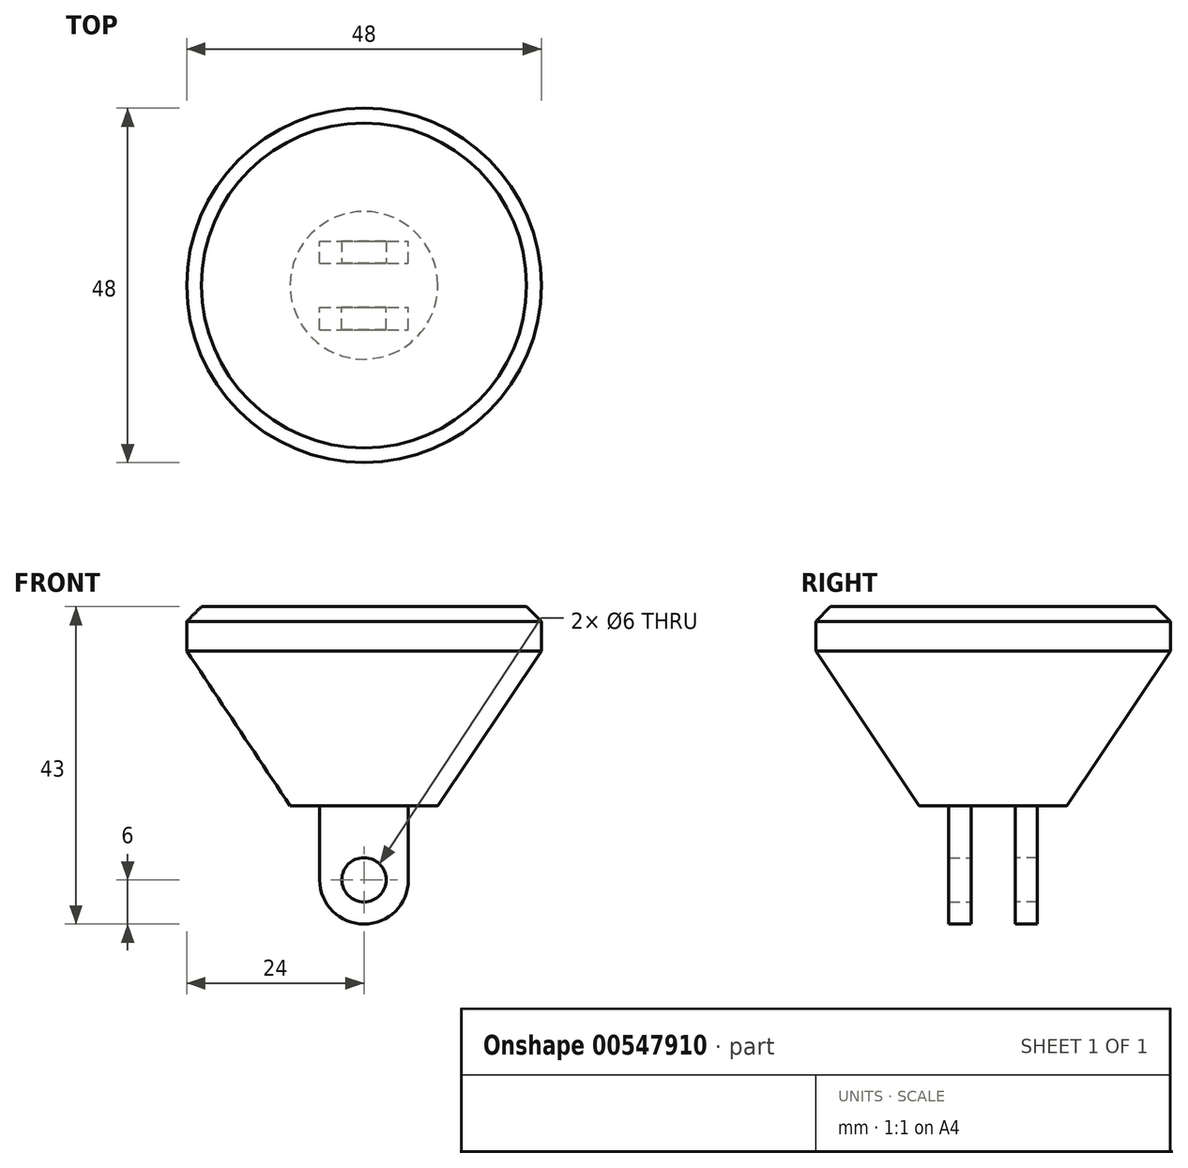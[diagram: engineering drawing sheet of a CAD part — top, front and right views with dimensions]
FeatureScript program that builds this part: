
annotation { "Feature Type Name" : "Feature", "Feature Type Description" : "" }
export const myFeature = defineFeature(function(context is Context, id is Id, definition is map)
    precondition{}
    {
        {
            var Q0;
            Q0=qCreatedBy(makeId("Front.planeOp"),FACE);
            var sketch = newSketch(context, id + "F0", { "sketchPlane" : qUnion([Q0])});
            skLineSegment(sketch, "E0", {"start": v(0, 0) * mm, "end": v(0, 27) * mm});
            skLineSegment(sketch, "E1", {"start": v(0, 27) * mm, "end": v(24, 27) * mm});
            skLineSegment(sketch, "E2", {"start": v(24, 27) * mm, "end": v(24, 21) * mm});
            skLineSegment(sketch, "E3", {"start": v(24, 21) * mm, "end": v(10, 0) * mm});
            skLineSegment(sketch, "E4", {"start": v(10, 0) * mm, "end": v(0, 0) * mm});
            skSolve(sketch);
        }
        {
            var Q0;
            Q0=makeQuery(id+"F0.imprint","IMPRINT",FACE,{"disambiguationData":[TD([[makeQuery(id+"F0.imprint","IMPRINT",EDGE,{"derivedFrom":sQuery(id+"F0.wireOp",EDGE,"E0")}),-1.0]])]});
            var Q1;
            Q1=sQuery(id+"F0.wireOp",EDGE,"E0");
            revolve(context, id + "F1", {"entities" : qUnion([Q0]), "axis" : qUnion([Q1]), "revolveType" : RevolveType.FULL});
        }
        {
            var Q0;
            Q0=qCreatedBy(makeId("Front.planeOp"),FACE);
            var sketch = newSketch(context, id + "F2", { "sketchPlane" : qUnion([Q0])});
            skLineSegment(sketch, "E5", {"start": v(6, 0) * mm, "end": v(6, -10) * mm});
            skArc(sketch, "E6", {"start": v(-6, -10) * mm, "mid": v(0, -16) * mm, "end": v(6, -10) * mm});
            skLineSegment(sketch, "E7", {"start": v(-6, -10) * mm, "end": v(-6, 0) * mm});
            skLineSegment(sketch, "E8", {"start": v(-6, 0) * mm, "end": v(6, 0) * mm});
            skSolve(sketch);
        }
        {
            var Q0;
            Q0=makeQuery(id+"F2.imprint","IMPRINT",FACE,{"disambiguationData":[TD([[makeQuery(id+"F2.imprint","IMPRINT",EDGE,{"derivedFrom":sQuery(id+"F2.wireOp",EDGE,"E5")}),-1.0]])]});
            extrude(context, id + "F3", {"entities" : qUnion([Q0]), "operationType" : NewBodyOperationType.ADD, "endBound" : BoundingType.SYMMETRIC, "depth" : 12 * mm, "offsetDistance" : 25 * mm});
        }
        {
            var Q0;
            Q0 = qSketchRegion(id + "F2", true);
            extrude(context, id + "F4", {"entities" : qUnion([Q0]), "operationType" : NewBodyOperationType.REMOVE, "endBound" : BoundingType.SYMMETRIC, "oppositeDirection" : true, "depth" : 6 * mm, "offsetDistance" : 25 * mm});
        }
        {
            var Q0;
            Q0=sQuery(id+"F2.wireOp",VERTEX,"E6.center");
            var Q1;
            Q1=makeQuery(id+"F1.opRevolve","SWEPT_BODY",BODY,{"disambiguationData":[OSD([sQuery(id+"F0.wireOp",EDGE,"E0"),sQuery(id+"F0.wireOp",EDGE,"E1"),sQuery(id+"F0.wireOp",EDGE,"E2"),sQuery(id+"F0.wireOp",EDGE,"E3"),sQuery(id+"F0.wireOp",EDGE,"E4")])]});
            hole(context, id + "F5", {"style" : HoleStyle.SIMPLE, "endStyle" : HoleEndStyle.THROUGH, "holeDiameter" : 6 * mm, "isTappedThrough" : true, "tappedDepth" : 12 * mm, "tapClearance" : 3, "locations" : qUnion([Q0]), "scope" : qUnion([Q1])});
        }
        {
            var Q0;
            Q0=sQuery(id+"F2.wireOp",VERTEX,"E6.center");
            var Q1;
            Q1=makeQuery(id+"F1.opRevolve","SWEPT_BODY",BODY,{"disambiguationData":[OSD([sQuery(id+"F0.wireOp",EDGE,"E0"),sQuery(id+"F0.wireOp",EDGE,"E1"),sQuery(id+"F0.wireOp",EDGE,"E2"),sQuery(id+"F0.wireOp",EDGE,"E3"),sQuery(id+"F0.wireOp",EDGE,"E4")])]});
            hole(context, id + "F6", {"style" : HoleStyle.SIMPLE, "endStyle" : HoleEndStyle.THROUGH, "oppositeDirection" : true, "holeDiameter" : 6 * mm, "isTappedThrough" : true, "tappedDepth" : 12 * mm, "tapClearance" : 3, "locations" : qUnion([Q0]), "scope" : qUnion([Q1])});
        }
        {
            var Q0;
            Q0=makeQuery(id+"F1.opRevolve","SWEPT_EDGE",EDGE,{"disambiguationData":[OSD([sQuery(id+"F0.wireOp",EDGE,"E1"),sQuery(id+"F0.wireOp",EDGE,"E2")])]});
            chamfer(context, id + "F7", {"entities" : qUnion([Q0]), "width" : 2 * mm, "tangentPropagation" : true});
        }
    });
